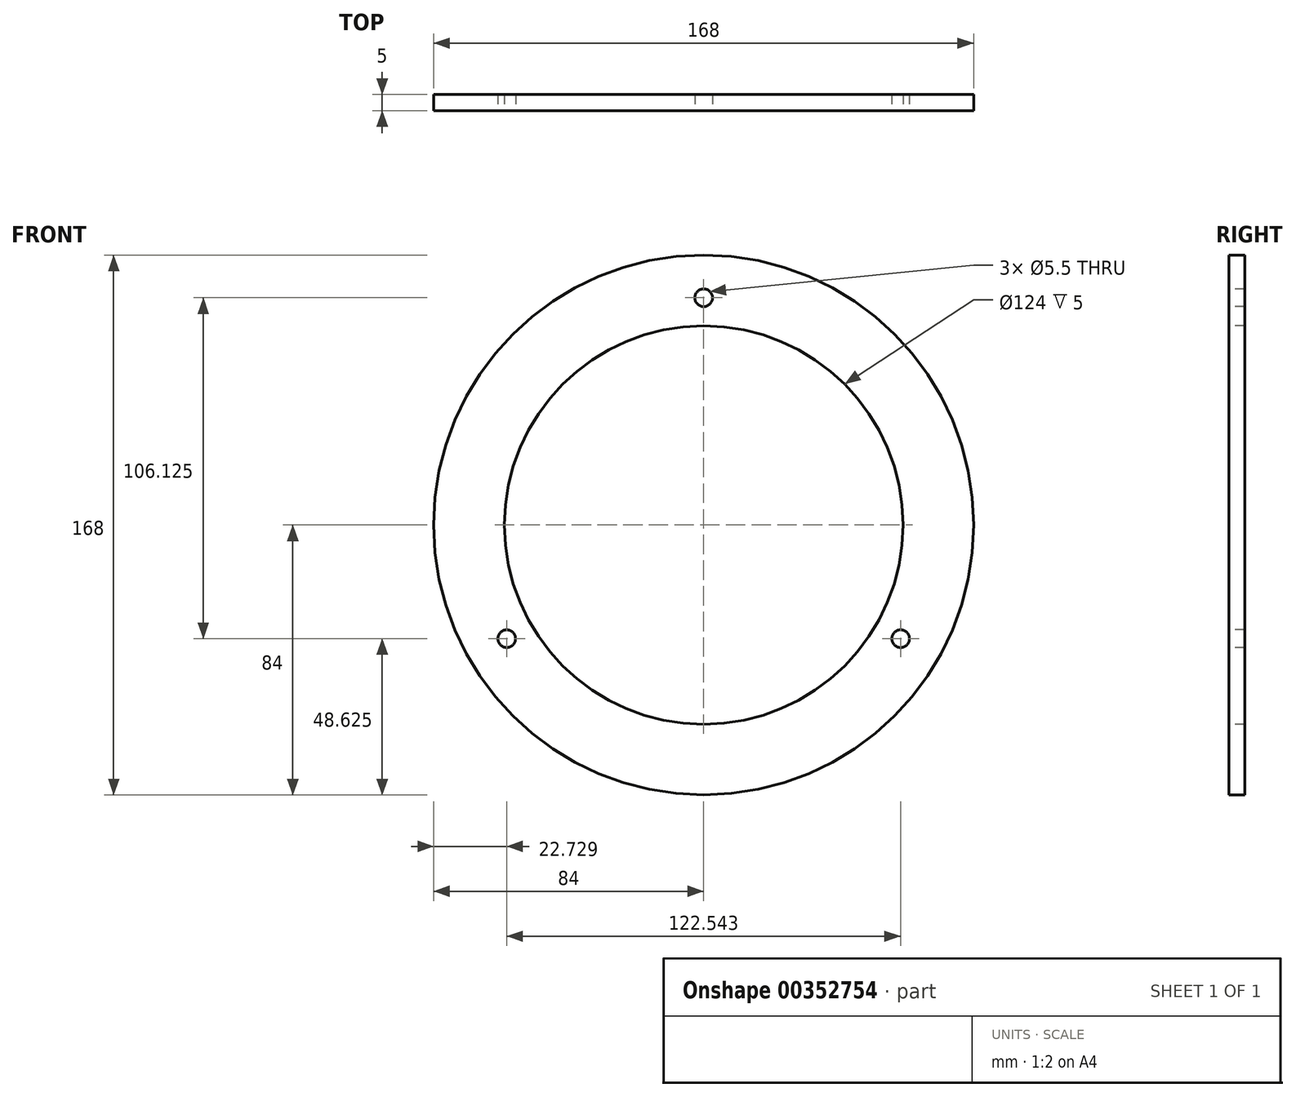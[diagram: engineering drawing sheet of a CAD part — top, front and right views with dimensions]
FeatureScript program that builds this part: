
annotation { "Feature Type Name" : "Feature", "Feature Type Description" : "" }
export const myFeature = defineFeature(function(context is Context, id is Id, definition is map)
    precondition{}
    {
        {
            var Q0;
            Q0=qCreatedBy(makeId("Front.planeOp"),FACE);
            var sketch = newSketch(context, id + "F0", { "sketchPlane" : qUnion([Q0])});
            skCircle(sketch, "E0", {"center": v(0, 0) * mm, "radius": 62 * mm});
            skCircle(sketch, "E1", {"center": v(0, 0) * mm, "radius": 84 * mm});
            skSolve(sketch);
        }
        {
            var Q0;
            Q0=makeQuery(id+"F0.imprint","IMPRINT",FACE,{"disambiguationData":[TD([[makeQuery(id+"F0.imprint","IMPRINT",EDGE,{"derivedFrom":sQuery(id+"F0.wireOp",EDGE,"E0")}),-1.0]])]});
            extrude(context, id + "F1", {"entities" : qUnion([Q0]), "oppositeDirection" : true, "depth" : 5 * mm});
        }
        {
            var Q0;
            Q0=makeQuery(id+"F1.opExtrude","CAP_FACE",FACE,{"disambiguationData":[OSD([sQuery(id+"F0.wireOp",EDGE,"E0"),sQuery(id+"F0.wireOp",EDGE,"E1")])],"isStart":true});
            var sketch = newSketch(context, id + "F2", { "sketchPlane" : qUnion([Q0])});
            skLineSegment(sketch, "E2", {"start": v(0, 84) * mm, "end": v(0, 62) * mm, "construction": true});
            skCircle(sketch, "E3", {"center": v(0, 70.75) * mm, "radius": 2.75 * mm});
            skCircle(sketch, "E4.1.0", {"center": v(-61.27, -35.37) * mm, "radius": 2.75 * mm});
            skCircle(sketch, "E4.2.0", {"center": v(61.27, -35.38) * mm, "radius": 2.75 * mm});
            skPoint(sketch, "E4.center", {"position": v(0, 0) * mm});
            skSolve(sketch);
        }
        {
            var Q0;
            Q0 = qSketchRegion(id + "F2", true);
            extrude(context, id + "F3", {"entities" : qUnion([Q0]), "operationType" : NewBodyOperationType.REMOVE, "endBound" : BoundingType.THROUGH_ALL, "oppositeDirection" : true, "depth" : 25 * mm});
        }
    });
